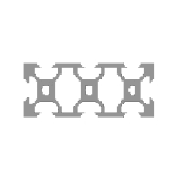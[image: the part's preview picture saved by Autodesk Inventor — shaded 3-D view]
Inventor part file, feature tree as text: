
AUTODESK INVENTOR PART (.ipt)
format: ipt  version: 2013 (Build 170138000, 138)  size: 242,176 bytes
history: native  units: mm
features: other x4, sketch x2, plane x1
ambient origin geometry x8: Origin, YZ Plane, XZ Plane, XY Plane, X Axis, Y Axis, Z Axis, Center Point
bodies: Solid1 (feature_tree), Body (feature_tree)
feature tree (7):
  other  "Driven Length"
  other  "Frame Generator"
  other  "Start Plane"
  other  "End Plane"
  sketch  "Sketch4"  dims[d0=10.0mm]
  plane  "Work Plane4"
  sketch  "Sketch5"  dims[d1=10.0mm d2=10.0mm d3=4.2mm d4=1.5mm d5=45.0deg d6=1.64mm d7=1.8mm d8=10.0mm d9=2.84mm d11=135.0deg d12=1.96mm d13=5.68mm d14=1.8mm d17=-0.0mm d18=475.0mm d19=0.13mm d20=0.0mm d23=90.0deg d22=475.0mm]
